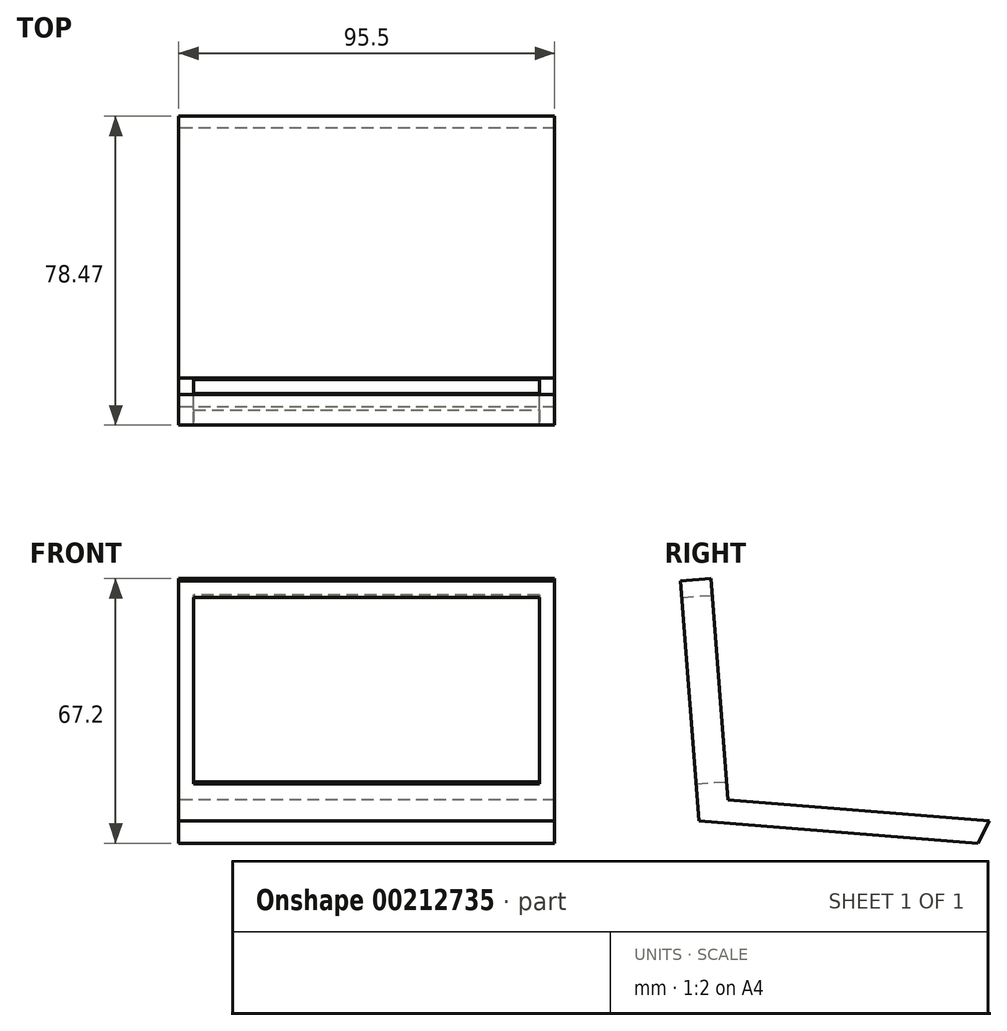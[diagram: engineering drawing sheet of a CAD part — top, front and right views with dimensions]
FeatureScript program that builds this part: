
annotation { "Feature Type Name" : "Feature", "Feature Type Description" : "" }
export const myFeature = defineFeature(function(context is Context, id is Id, definition is map)
    precondition{}
    {
        {
            var Q0;
            Q0=qCreatedBy(makeId("Right.planeOp"),FACE);
            var sketch = newSketch(context, id + "F0", { "sketchPlane" : qUnion([Q0])});
            skLineSegment(sketch, "E0", {"start": v(-27.23, -24.7) * mm, "end": v(-31.85, 36.24) * mm});
            skLineSegment(sketch, "E1", {"start": v(-31.85, 36.24) * mm, "end": v(-24.12, 36.82) * mm});
            skLineSegment(sketch, "E2", {"start": v(-24.12, 36.82) * mm, "end": v(-19.86, -19.37) * mm});
            skLineSegment(sketch, "E3", {"start": v(-27.23, -24.7) * mm, "end": v(43.65, -30.38) * mm});
            skLineSegment(sketch, "E4", {"start": v(-19.86, -19.37) * mm, "end": v(46.62, -24.7) * mm});
            skLineSegment(sketch, "E5", {"start": v(46.62, -24.7) * mm, "end": v(43.65, -30.38) * mm});
            skSolve(sketch);
        }
        {
            var Q0;
            Q0=makeQuery(id+"F0.imprint","IMPRINT",FACE,{"disambiguationData":[TD([[makeQuery(id+"F0.imprint","IMPRINT",EDGE,{"derivedFrom":sQuery(id+"F0.wireOp",EDGE,"E0")}),-1.0]])]});
            extrude(context, id + "F1", {"entities" : qUnion([Q0]), "endBound" : BoundingType.SYMMETRIC, "depth" : 95.5 * mm});
        }
        {
            var Q0;
            Q0=makeQuery(id+"F1.opExtrude","SWEPT_FACE",FACE,{"disambiguationData":[OSD([sQuery(id+"F0.wireOp",EDGE,"E2")])]});
            var sketch = newSketch(context, id + "F2", { "sketchPlane" : qUnion([Q0])});
            skLineSegment(sketch, "E6.bottom", {"start": v(-43.84, 34.33) * mm, "end": v(43.93, 34.33) * mm});
            skLineSegment(sketch, "E6.top", {"start": v(-43.84, -13.18) * mm, "end": v(43.93, -13.18) * mm});
            skLineSegment(sketch, "E6.left", {"start": v(-43.84, 34.33) * mm, "end": v(-43.84, -13.18) * mm});
            skLineSegment(sketch, "E6.right", {"start": v(43.93, 34.33) * mm, "end": v(43.93, -13.18) * mm});
            skSolve(sketch);
        }
        {
            var Q0;
            Q0=makeQuery(id+"F2.imprint","IMPRINT",FACE,{"disambiguationData":[TD([[makeQuery(id+"F2.imprint","IMPRINT",EDGE,{"derivedFrom":sQuery(id+"F2.wireOp",EDGE,"E6.bottom")}),-1.0]])]});
            extrude(context, id + "F3", {"entities" : qUnion([Q0]), "operationType" : NewBodyOperationType.REMOVE, "oppositeDirection" : true, "depth" : 32 * mm});
        }
    });
